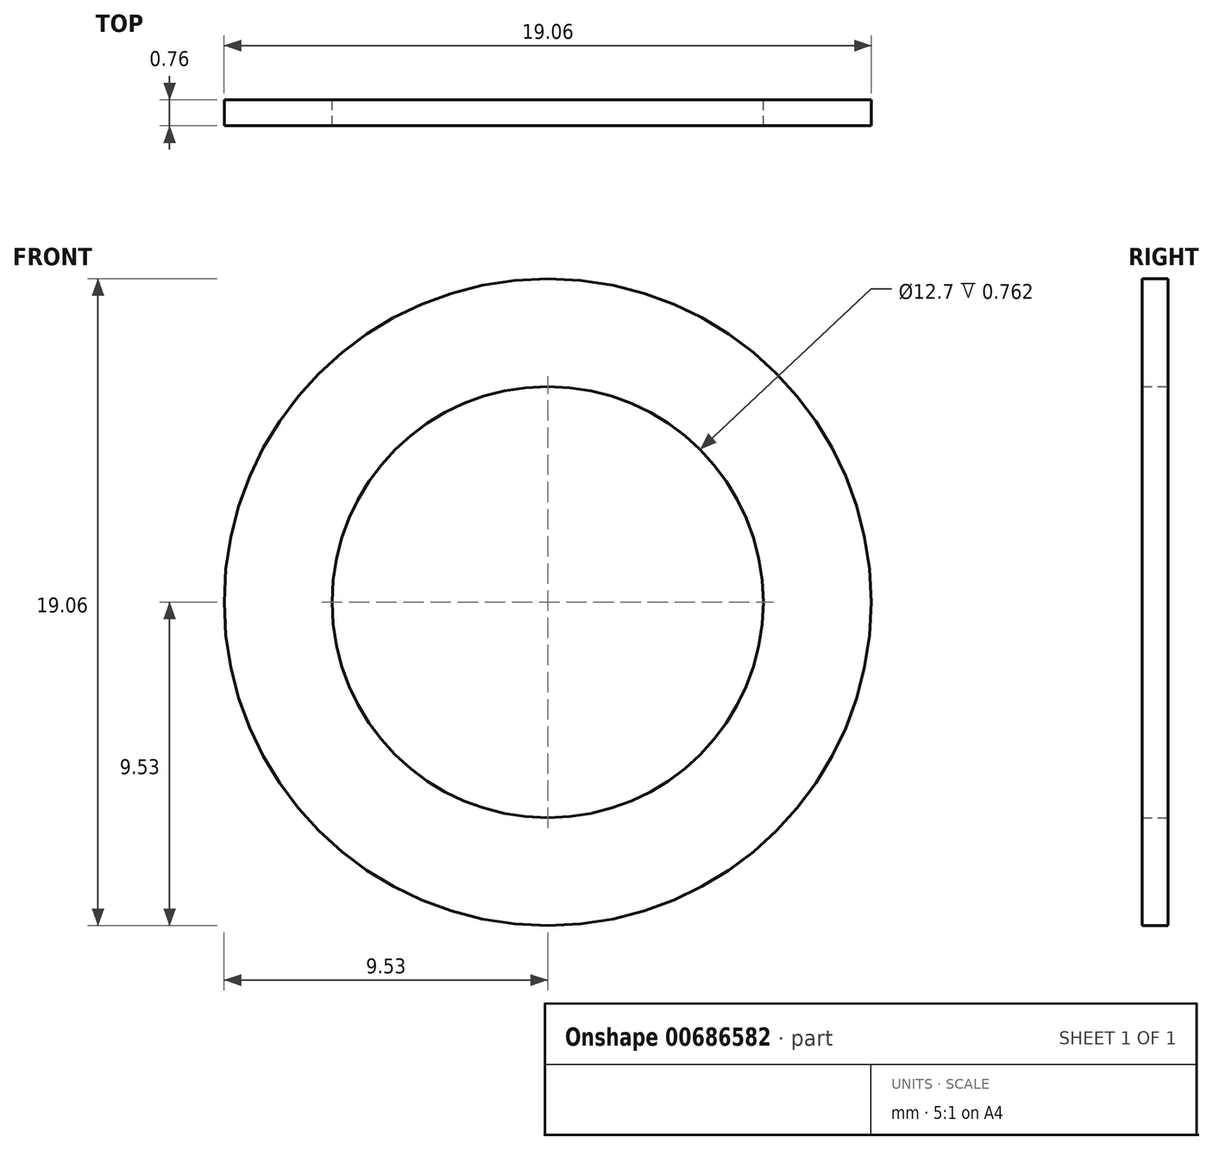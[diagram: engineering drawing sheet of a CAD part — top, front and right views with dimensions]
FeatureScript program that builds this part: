
annotation { "Feature Type Name" : "Feature", "Feature Type Description" : "" }
export const myFeature = defineFeature(function(context is Context, id is Id, definition is map)
    precondition{}
    {
        {
            var Q0;
            Q0=qCreatedBy(makeId("Front.planeOp"),FACE);
            var sketch = newSketch(context, id + "F0", { "sketchPlane" : qUnion([Q0])});
            skCircle(sketch, "E0", {"center": v(0, 0) * mm, "radius": 9.53 * mm});
            skCircle(sketch, "E1", {"center": v(0, 0) * mm, "radius": 6.35 * mm});
            skSolve(sketch);
        }
        {
            var Q0;
            Q0=makeQuery(id+"F0.imprint","IMPRINT",FACE,{"disambiguationData":[TD([[makeQuery(id+"F0.imprint","IMPRINT",EDGE,{"derivedFrom":sQuery(id+"F0.wireOp",EDGE,"E0")}),1.0]])]});
            extrude(context, id + "F1", {"entities" : qUnion([Q0]), "depth" : 0.76 * mm, "offsetDistance" : 25.4 * mm});
        }
    });
